# Revit family: PRD_AR_MxrTps_F7EElectronicPillarMixer_F7EM1001_F7EM1002
name_source: partatom
category: Plumbing Fixtures
units: mm (PartAtom-declared; Revit-internal decimal feet)

## family parameters
Always vertical = Yes
Cut with Voids When Loaded = No
Enable Cutting in Views = No
Maintain Annotation Orientation = No
OmniClass Number = 23.45.55.17
OmniClass Title = Mixing Faucets
Part Type = Normal
Room Calculation Point = No
Round Connector Dimension = Use Diameter
Shared = No
Work Plane-Based = Yes

## types (2) — shared parameters
AccentColour = None
AssetType = Fixed
BasicColour = Stainless steel-look
BodyMaterial = PRD_AR_StainlessSteel_Brushed
Category = Pr_40_20_87_55, Mixer taps
CloseOffRating = 0.0 Pa
Color = stainless steel-look
CompatibleA3000Open = Yes
Default Elevation = 1219 mm
DefaultAutomaticHygieneFlush = 24h after the last activity
Depressurised = No
DiameterNominal = DN15
Export Type to IFC As = IfcValveType
FaucetFunction = MIXED
FaucetOperation = SELFCLOSING
FaucetTopDescription = opto-electronically controlled
FaucetType = PILLAR
Finish = brushed surface
FlowColdWater = 0.0 L/s
FlowHotWater = 0.0 L/s
FunctionalPrinciple = electronic self-closing
HygieneFlushing = Yes
IfcExportAs = IfcValveType
IfcExportType = FAUCET
InletSize = G 3/8
LockingMechanism = Top section, non-ceramic
Manufacturer = KWC Group Management AG
ManufacturerName = KWC Group Management AG
ManufacturerURL = www.kwc-professional.com
Material = stainless steel
MaterialFitting = Stainless Steel
MinimumFlowPressure = 1 bar
NBSDescription = Taps and water supply fittings for sinks
NBSReference = 45-35-70/345
Parameterization = Remote Control
PopUpWasteSet = No
PositionOfPowerConnection = From Bottom
PowerSupplyConnection = 6,75 / 12 V DC / A3000 open
ProductInformation = http://pim.kwc.com
ProtectiveShutdown = Yes
Shape = Pillar tap
Size = 15
SoundInsulation = No
Spout = Fixed
Status = New
SurfaceFinishFitting = Brushed
SurfaceTreatmentFitting = Brushed
TemperatureLimit = Yes
TestPressure = 0.0 Pa
ThermalDisinfection = No
Type IFC Predefined Type = FAUCET
TypeOfMixing = Yes
TypeOfMounting = Tap Hole
TypeOfOperation = Sensor Operation
TypeOfPowerSupply = Other
TypeOfSensor = Opto-electronic sensor
TypeOfTap = Pillar Tap
URL = www.kwc-professional.com
Uniclass2015Code = Pr_40_20_87_55
Uniclass2015Title = Mixer taps
Uniclass2015Version = Products v1.36
ValveMechanism = OTHER
ValveOperation = SOLENOID
ValvePattern = STRAIGHT_3_PORT
Version = 1
Voltage = 12 V
WaterConnection = Hose (gland nut)
WithBackflowPreventer = Yes
WithFilter = Yes
WithRosettesOrCoverPlate = No
WithTransformer = No
WorkingPressure = 0.0 Pa
zero-valued in all types: FlowCoefficient, NominalDepth, NominalWidth

## per-type parameters (varying)
| type | BIMObjectName | Description | F7EM1001 | F7EM1002 | Features | ModelNumber | Name | NominalHeight |
| F7EM1001 | PRD_AR_MixerTaps_F7EElectronicPillarMixer_F7EM1001 | F7E-Mix pillar mixer DN 15 for sanitary facilities, opto-electronically controlled. For connection to hot and cold water via hoses with integrated backflow preventers and strainers. Control electronics, solenoid valve and sensor in stainless steel housing, brushed surface, outlet height 115 mm and projection 125 mm. Stainless steel temperature lever with adjustable, turn-proof temperature stop. Angle-adjustable and anti-theft aerator with integrated flow regulator 5.7 l/min. Activated water hygiene flushing 24 hours after last activation, safety switch-off with continuous reflection and saving of statistical data. With option for parameterization and communication via optional bidirectional remote control or C module with the necessary app. Optionally for battery operation with battery compartment including 6 V lithium battery (CR-P2) per fitting, for installation below the washbasin, or for separate power supply via power supply unit 6.75 V/12 V DC or AQUA 3000 open system accessories.

Battery compartment including battery or power supply unit with extension cable must be ordered separately. | Yes | No | For connection to hot and cold water via hoses with integrated backflow preventers and strainers. Control electronics, solenoid valve and sensor in stainless steel housing, brushed surface, outlet height 115 mm and projection 125 mm. | 3600001257 | F7E Electronic pillar mixer F7EM1001 | 165 mm  [stored 0.541339 ft] |
| F7EM1002 | PRD_AR_MixerTaps_F7EElectronicPillarMixer_F7EM1002 | F7E-Mix pillar mixer DN 15 for sanitary facilities, opto-electronically controlled. For connection to hot and cold water via hoses with integrated backflow preventers and strainers. Control electronics, solenoid valve and sensor in stainless steel housing, brushed surface, outlet height 245 mm and projection 180 mm. Stainless steel temperature lever with adjustable, turn-proof temperature stop. Angle-adjustable and anti-theft aerator with integrated flow regulator 5.7 l/min. Activated water hygiene flushing 24 hours after last activation, safety switch-off with continuous reflection and saving of statistical data. With option for parameterization and communication via optional bidirectional remote control or C module with the necessary app. Optionally for battery operation with battery compartment including 6 V lithium battery (CR-P2) per fitting, for installation below the washbasin, or for separate power supply via power supply unit 6.75 V/12 V DC or AQUA 3000 open system accessories.

Battery compartment including battery or power supply unit with extension cable must be ordered separately. | No | Yes | For connection to hot and cold water via hoses with integrated backflow preventers and strainers. Control electronics, solenoid valve and sensor in stainless steel housing, brushed surface, outlet height 245 mm and projection 180 mm. | 3600001259 | F7E Electronic pillar mixer F7EM1002 | 295 mm  [stored 0.967848 ft] |

note: column(s) folded — value = type name in every type: Model, ModelReference

note: [stored X ft] marks values corroborated as IEEE doubles in the binary element streams (Revit-internal decimal feet)

## geometry (parser evidence)
native form markers: Sweep x6
no freeform markers — native parametric forms only
